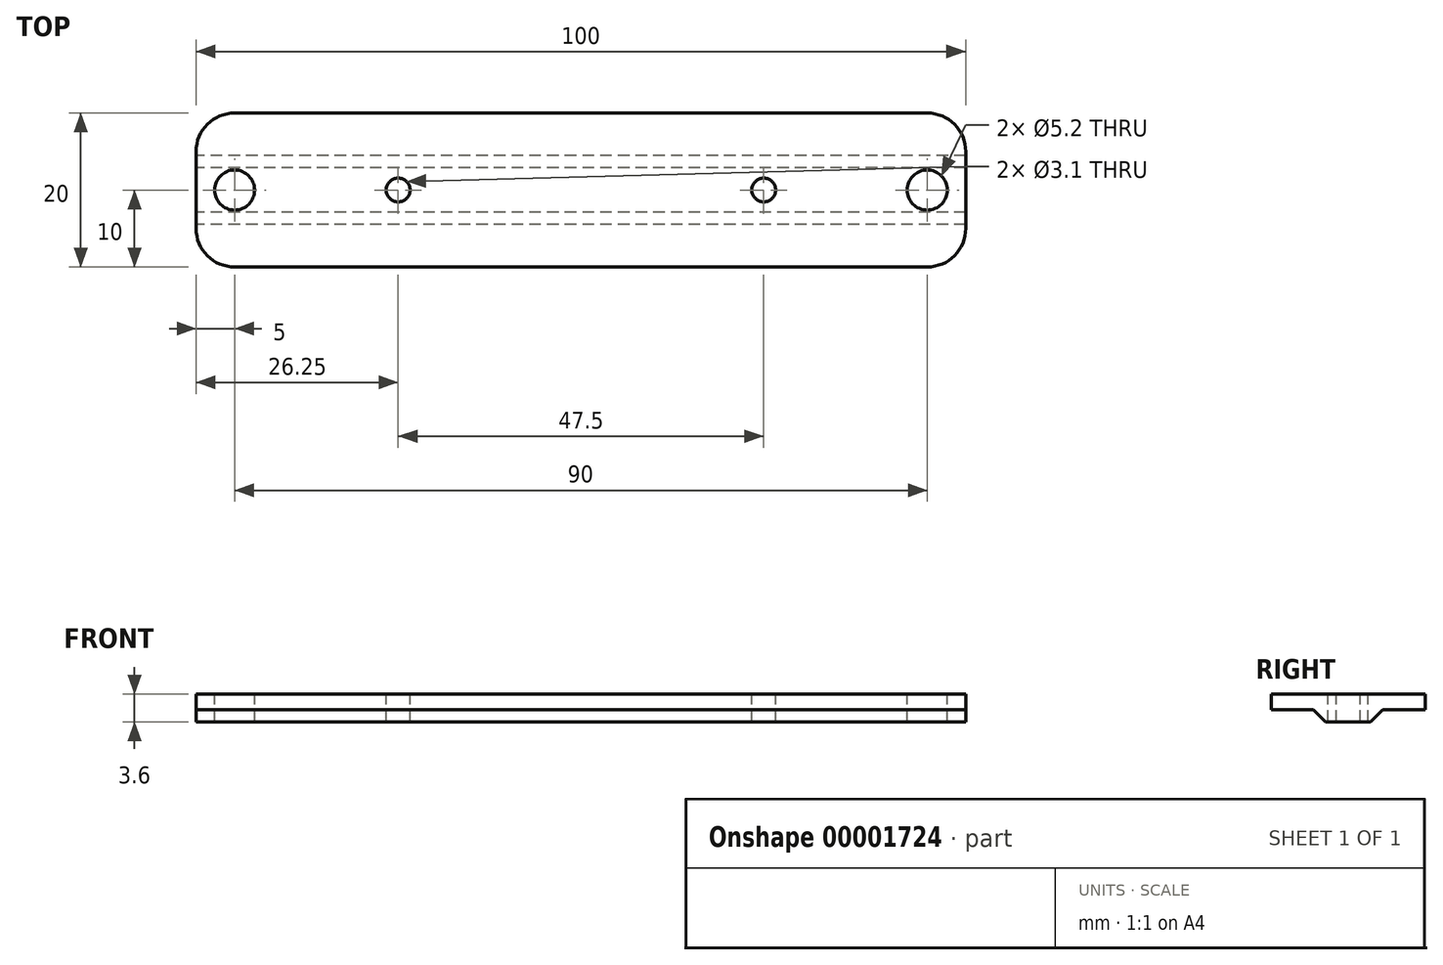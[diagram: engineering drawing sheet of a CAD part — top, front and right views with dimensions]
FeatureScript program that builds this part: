
annotation { "Feature Type Name" : "Feature", "Feature Type Description" : "" }
export const myFeature = defineFeature(function(context is Context, id is Id, definition is map)
    precondition{}
    {
        {
            var Q0;
            Q0=qCreatedBy(makeId("Right.planeOp"),FACE);
            var sketch = newSketch(context, id + "F0", { "sketchPlane" : qUnion([Q0])});
            skLineSegment(sketch, "E0", {"start": v(4.5, 0) * mm, "end": v(2.9, -1.6) * mm});
            skLineSegment(sketch, "E1", {"start": v(2.9, -1.6) * mm, "end": v(-2.9, -1.6) * mm});
            skLineSegment(sketch, "E2", {"start": v(-2.9, -1.6) * mm, "end": v(-4.5, 0) * mm});
            skPoint(sketch, "E3", {"position": v(0, 0) * mm});
            skLineSegment(sketch, "E4", {"start": v(-4.5, 0) * mm, "end": v(-10, 0) * mm});
            skLineSegment(sketch, "E5", {"start": v(-10, 0) * mm, "end": v(-10, 2) * mm});
            skLineSegment(sketch, "E6", {"start": v(-10, 2) * mm, "end": v(10, 2) * mm});
            skLineSegment(sketch, "E7", {"start": v(10, 2) * mm, "end": v(10, 0) * mm});
            skLineSegment(sketch, "E8", {"start": v(10, 0) * mm, "end": v(4.5, 0) * mm});
            skPoint(sketch, "E9", {"position": v(0, 2) * mm});
            skSolve(sketch);
        }
        {
            var Q0;
            Q0 = qSketchRegion(id + "F0", true);
            extrude(context, id + "F1", {"entities" : qUnion([Q0]), "depth" : 100 * mm});
        }
        {
            var Q0;
            Q0=makeQuery(id+"F1.opExtrude","SWEPT_FACE",FACE,{"disambiguationData":[OSD([sQuery(id+"F0.wireOp",EDGE,"E6")])]});
            var sketch = newSketch(context, id + "F2", { "sketchPlane" : qUnion([Q0])});
            skCircle(sketch, "E10", {"center": v(5, 0) * mm, "radius": 2.6 * mm});
            skCircle(sketch, "E11", {"center": v(95, 0) * mm, "radius": 2.6 * mm});
            skCircle(sketch, "E12", {"center": v(26.25, 0) * mm, "radius": 1.55 * mm});
            skCircle(sketch, "E13", {"center": v(73.75, 0) * mm, "radius": 1.55 * mm});
            skLineSegment(sketch, "E14", {"start": v(5, 0) * mm, "end": v(26.25, 0) * mm, "construction": true});
            skLineSegment(sketch, "E15", {"start": v(73.75, 0) * mm, "end": v(95, 0) * mm, "construction": true});
            skSolve(sketch);
        }
        {
            var Q0;
            Q0 = qSketchRegion(id + "F2", true);
            extrude(context, id + "F3", {"entities" : qUnion([Q0]), "operationType" : NewBodyOperationType.REMOVE, "endBound" : BoundingType.THROUGH_ALL, "oppositeDirection" : true, "depth" : 25 * mm});
        }
        {
            var Q0;
            Q0=makeQuery(id+"F1.opExtrude","CAP_EDGE",EDGE,{"disambiguationData":[OSD([sQuery(id+"F0.wireOp",EDGE,"E5")])],"isStart":false});
            var Q1;
            Q1=makeQuery(id+"F1.opExtrude","CAP_EDGE",EDGE,{"disambiguationData":[OSD([sQuery(id+"F0.wireOp",EDGE,"E7")])],"isStart":false});
            var Q2;
            Q2=makeQuery(id+"F1.opExtrude","CAP_EDGE",EDGE,{"disambiguationData":[OSD([sQuery(id+"F0.wireOp",EDGE,"E5")])],"isStart":true});
            var Q3;
            Q3=makeQuery(id+"F1.opExtrude","CAP_EDGE",EDGE,{"disambiguationData":[OSD([sQuery(id+"F0.wireOp",EDGE,"E7")])],"isStart":true});
            fillet(context, id + "F4", {"entities" : qUnion([Q0, Q1, Q2, Q3]), "radius" : 5 * mm, "tangentPropagation" : true, "allowEdgeOverflow" : false});
        }
    });
